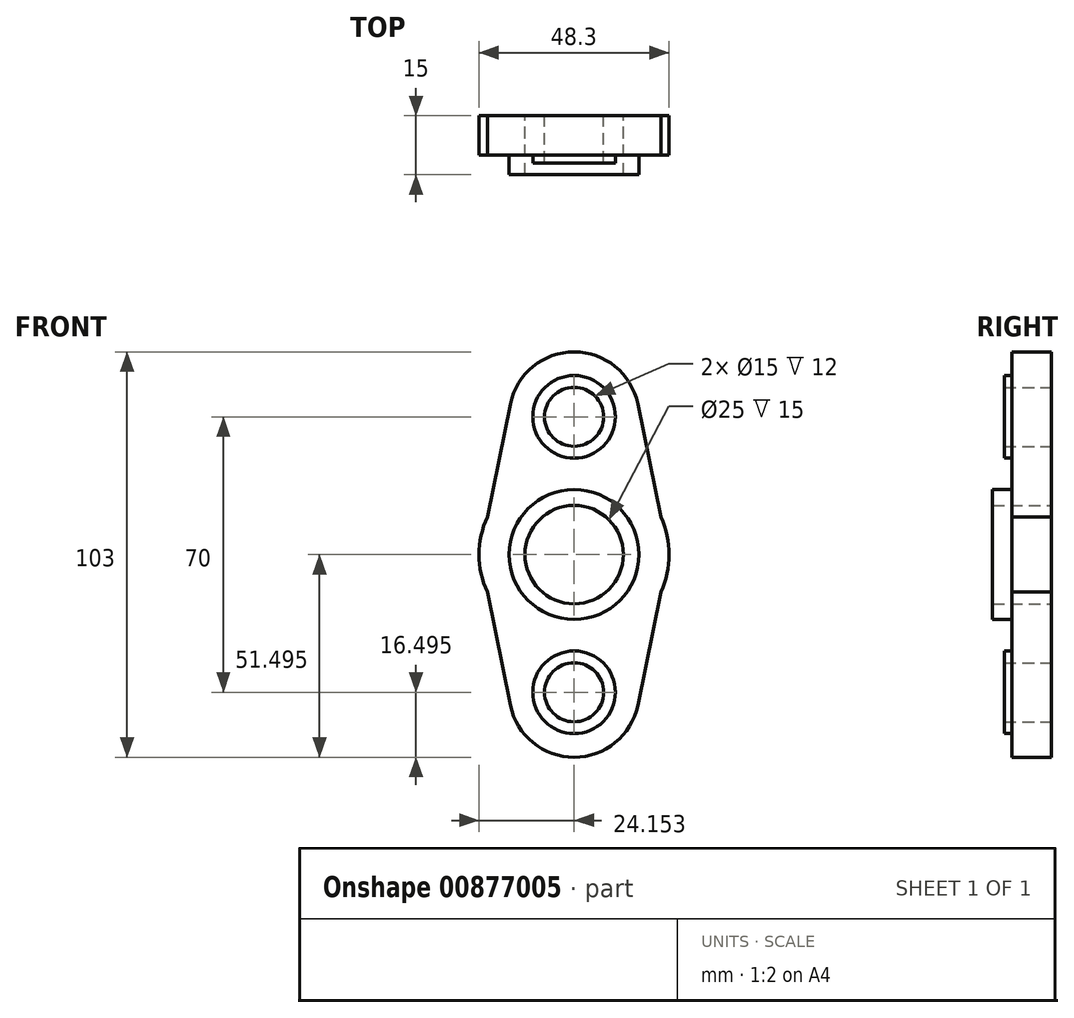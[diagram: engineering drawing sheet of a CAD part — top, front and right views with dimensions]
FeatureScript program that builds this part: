
annotation { "Feature Type Name" : "Feature", "Feature Type Description" : "" }
export const myFeature = defineFeature(function(context is Context, id is Id, definition is map)
    precondition{}
    {
        {
            var Q0;
            Q0=qCreatedBy(makeId("Front.planeOp"),FACE);
            var sketch = newSketch(context, id + "F0", { "sketchPlane" : qUnion([Q0])});
            skCircle(sketch, "E0", {"center": v(-47.36, 65.09) * mm, "radius": 12.5 * mm});
            skCircle(sketch, "E1", {"center": v(-47.36, 100.09) * mm, "radius": 7.5 * mm});
            skCircle(sketch, "E2", {"center": v(-47.36, 30.09) * mm, "radius": 7.5 * mm});
            skCircle(sketch, "E3", {"center": v(-47.36, 65.09) * mm, "radius": 16.5 * mm});
            skCircle(sketch, "E4", {"center": v(-47.36, 100.09) * mm, "radius": 10.5 * mm});
            skCircle(sketch, "E5", {"center": v(-47.36, 30.09) * mm, "radius": 10.5 * mm});
            skArc(sketch, "E6", {"start": v(-31.2, 103.39) * mm, "mid": v(-47.36, 116.59) * mm, "end": v(-63.52, 103.39) * mm});
            skArc(sketch, "E7", {"start": v(-63.52, 26.79) * mm, "mid": v(-47.36, 13.59) * mm, "end": v(-31.2, 26.79) * mm});
            skLineSegment(sketch, "E8", {"start": v(-69.4, 55.59) * mm, "end": v(-63.52, 26.79) * mm});
            skLineSegment(sketch, "E9", {"start": v(-31.2, 26.79) * mm, "end": v(-25.31, 55.59) * mm});
            skLineSegment(sketch, "E10", {"start": v(-31.2, 103.39) * mm, "end": v(-25.3, 74.55) * mm});
            skLineSegment(sketch, "E11", {"start": v(-63.52, 103.39) * mm, "end": v(-69.4, 74.59) * mm});
            skArc(sketch, "E12.trimOffspring", {"start": v(-69.4, 74.59) * mm, "mid": v(-71.5, 65.09) * mm, "end": v(-69.4, 55.59) * mm});
            skArc(sketch, "E13.trimOffspring", {"start": v(-25.31, 55.59) * mm, "mid": v(-23.2, 65.09) * mm, "end": v(-25.31, 74.59) * mm});
            skSolve(sketch);
        }
        {
            var Q0;
            Q0=makeQuery(id+"F0.imprint","IMPRINT",FACE,{"disambiguationData":[TD([[makeQuery(id+"F0.imprint","IMPRINT",EDGE,{"derivedFrom":sQuery(id+"F0.wireOp",EDGE,"E0")}),-1.0]])]});
            extrude(context, id + "F1", {"entities" : qUnion([Q0]), "depth" : 15 * mm, "offsetDistance" : 25 * mm});
        }
        {
            var Q0;
            Q0=makeQuery(id+"F0.imprint","IMPRINT",FACE,{"disambiguationData":[TD([[makeQuery(id+"F0.imprint","IMPRINT",EDGE,{"derivedFrom":sQuery(id+"F0.wireOp",EDGE,"E3")}),-1.0]])]});
            extrude(context, id + "F2", {"entities" : qUnion([Q0]), "operationType" : NewBodyOperationType.ADD, "depth" : 10 * mm, "offsetDistance" : 25 * mm});
        }
        {
            var Q0;
            Q0=makeQuery(id+"F0.imprint","IMPRINT",FACE,{"disambiguationData":[TD([[makeQuery(id+"F0.imprint","IMPRINT",EDGE,{"derivedFrom":sQuery(id+"F0.wireOp",EDGE,"E1")}),-1.0]])]});
            var Q1;
            Q1=makeQuery(id+"F0.imprint","IMPRINT",FACE,{"disambiguationData":[TD([[makeQuery(id+"F0.imprint","IMPRINT",EDGE,{"derivedFrom":sQuery(id+"F0.wireOp",EDGE,"E2")}),-1.0]])]});
            extrude(context, id + "F3", {"entities" : qUnion([Q0, Q1]), "operationType" : NewBodyOperationType.ADD, "depth" : 12 * mm, "offsetDistance" : 25 * mm});
        }
    });
